# Revit family: SW200i_Surface Applied Pair Egress Swing Door Operator
name_source: partatom
category: Generic Models
revit_build: Autodesk Revit 2014 (Build: 20130308_1515(x64)
units: mm (PartAtom-declared; Revit-internal decimal feet)

## types (1)
- SW200i_Surface Applied Pair Egress Swing Door Operator
    BIMobject category = Swing Doors
    Closed Door Axis Distance = 1' - 0"
    Date of publishing = 2015-02-23
    Depth = 0.00
    Edition number = 1
    Header Length = 6' - 0"
    Header Material = Clear Anodized
    IFC Classification = Door
    Manufacturer name = Besam-North America
    Material main = Aluminium
    Nominal height = 0.00
    Nominal width = 0.00
    Opened Door Axis Distance = 0' - 0"
    Operator Arm Material = Clear Anodized
    Product Guid = a6d7597d-b5c2-4f9e-8316-3faa01ef08e4
    Product SKU = SW200i_SM
    Product data url = http://besam-na.bimobject.com
    Product family = Swing
    Product group = Surface Mount
    Pull Arm Guide Offset = 0' - 4 1/2"
    QR code = http://besam-na.bimobject.com
    UNSPSC Code = 30171511
    Uniclass 1.4 Code = L81323
    Uniclass 1.4 Description = Swings
    Weight Net (Kg) = 0

## geometry (parser evidence)
native form markers: Blend x2, Sweep x23
no freeform markers — native parametric forms only
